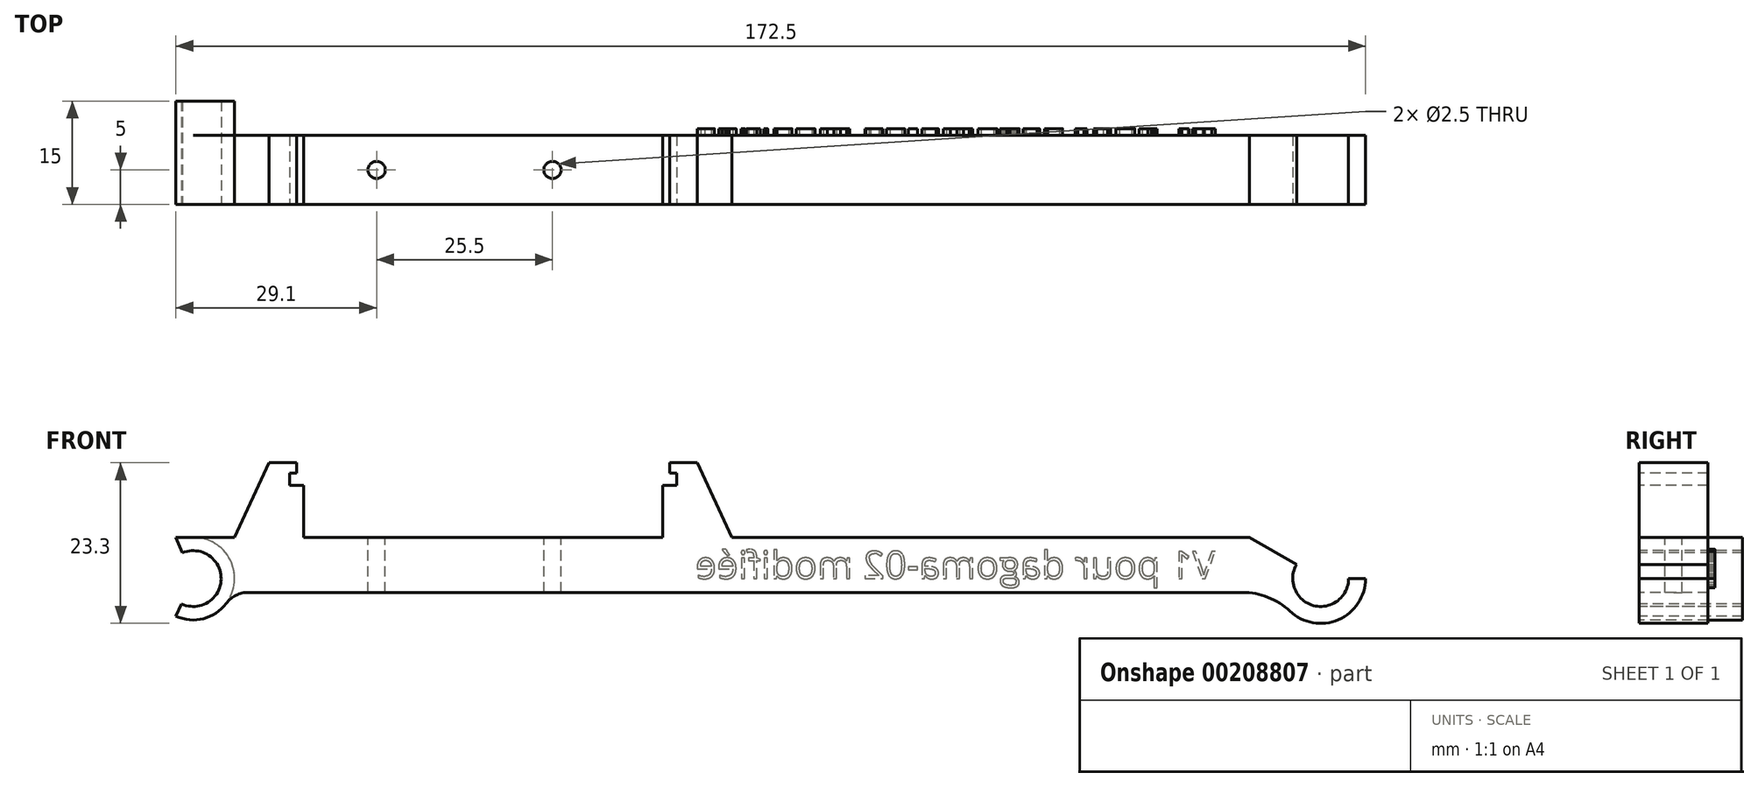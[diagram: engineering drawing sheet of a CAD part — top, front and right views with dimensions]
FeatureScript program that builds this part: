
annotation { "Feature Type Name" : "Feature", "Feature Type Description" : "" }
export const myFeature = defineFeature(function(context is Context, id is Id, definition is map)
    precondition{}
    {
        {
            var Q0;
            Q0=qCreatedBy(makeId("Front.planeOp"),FACE);
            var sketch = newSketch(context, id + "F0", { "sketchPlane" : qUnion([Q0])});
            skArc(sketch, "E0", {"start": v(-1.69, -3.68) * mm, "mid": v(4.05, -0.07) * mm, "end": v(-1.56, 3.74) * mm});
            skArc(sketch, "E1", {"start": v(-2.5, -5.45) * mm, "mid": v(1.48, -5.82) * mm, "end": v(4.8, -3.6) * mm});
            skLineSegment(sketch, "E2", {"start": v(-2.5, 6) * mm, "end": v(6, 6) * mm});
            skLineSegment(sketch, "E3", {"start": v(8, -2) * mm, "end": v(157.32, -2) * mm});
            skLineSegment(sketch, "E4", {"start": v(-1.56, 3.74) * mm, "end": v(-2.5, 6) * mm});
            skLineSegment(sketch, "E5", {"start": v(-1.69, -3.68) * mm, "end": v(-2.5, -5.45) * mm});
            skArc(sketch, "E6.filletArc", {"start": v(8, -2) * mm, "mid": v(6.21, -2.42) * mm, "end": v(4.8, -3.6) * mm});
            skArc(sketch, "E7", {"start": v(0, 6) * mm, "mid": v(5.37, 2.68) * mm, "end": v(4.8, -3.6) * mm});
            skLineSegment(sketch, "E8", {"start": v(16, 6) * mm, "end": v(16, 13.5) * mm});
            skLineSegment(sketch, "E9", {"start": v(16, 13.5) * mm, "end": v(14, 13.5) * mm});
            skLineSegment(sketch, "E10", {"start": v(14, 13.5) * mm, "end": v(14, 15.3) * mm});
            skLineSegment(sketch, "E11", {"start": v(14, 15.3) * mm, "end": v(15, 15.3) * mm});
            skLineSegment(sketch, "E12", {"start": v(15, 15.3) * mm, "end": v(15, 16.8) * mm});
            skLineSegment(sketch, "E13", {"start": v(15, 16.8) * mm, "end": v(11, 16.8) * mm});
            skLineSegment(sketch, "E14", {"start": v(11, 16.8) * mm, "end": v(6, 6) * mm});
            skLineSegment(sketch, "E15", {"start": v(68.1, 6) * mm, "end": v(68.1, 13.5) * mm});
            skLineSegment(sketch, "E16", {"start": v(68.1, 13.5) * mm, "end": v(70.1, 13.5) * mm});
            skLineSegment(sketch, "E17", {"start": v(70.1, 13.5) * mm, "end": v(70.1, 15.3) * mm});
            skLineSegment(sketch, "E18", {"start": v(70.1, 15.3) * mm, "end": v(69.1, 15.3) * mm});
            skLineSegment(sketch, "E19", {"start": v(69.1, 15.3) * mm, "end": v(69.1, 16.8) * mm});
            skLineSegment(sketch, "E20", {"start": v(69.1, 16.8) * mm, "end": v(73.1, 16.8) * mm});
            skLineSegment(sketch, "E21", {"start": v(73.1, 16.8) * mm, "end": v(78.1, 6) * mm});
            skLineSegment(sketch, "E22.trimOffspring", {"start": v(16, 6) * mm, "end": v(68.1, 6) * mm});
            skLineSegment(sketch, "E23.trimOffspring", {"start": v(78.1, 6) * mm, "end": v(153.2, 6) * mm});
            skLineSegment(sketch, "E24", {"start": v(167.55, 0) * mm, "end": v(170, 0) * mm});
            skArc(sketch, "E25", {"start": v(160, 2.04) * mm, "mid": v(162.44, -3.91) * mm, "end": v(167.55, 0) * mm});
            skArc(sketch, "E26", {"start": v(157.32, -2) * mm, "mid": v(164.51, -6.42) * mm, "end": v(170, 0) * mm});
            skLineSegment(sketch, "E27", {"start": v(160, 2.04) * mm, "end": v(153.2, 6) * mm});
            skSolve(sketch);
        }
        {
            var Q0;
            Q0=makeQuery(id+"F0.imprint","IMPRINT",FACE,{"disambiguationData":[TD([[makeQuery(id+"F0.imprint","IMPRINT",EDGE,{"derivedFrom":sQuery(id+"F0.wireOp",EDGE,"E3")}),1.0]])]});
            extrude(context, id + "F1", {"entities" : qUnion([Q0]), "oppositeDirection" : true, "depth" : 10 * mm});
        }
        {
            var Q0;
            {var subQ6=sQuery(id+"F0.wireOp",EDGE,"E0");Q0=makeQuery(id+"F0.imprint","IMPRINT",FACE,{"disambiguationData":[TD([[makeQuery(id+"F0.imprint","IMPRINT",EDGE,{"derivedFrom":subQ6}),-1.0]])]});}
            var Q1;
            {var subQ6=sQuery(id+"F0.wireOp",EDGE,"9NDdW5uR-K7Dr-FAK1-duLJ-1dfglirlA18k");Q1=makeQuery(id+"F0.imprint","IMPRINT",FACE,{"disambiguationData":[TD([[makeQuery(id+"F0.imprint","IMPRINT",EDGE,{"derivedFrom":subQ6}),-1.0]])]});}
            extrude(context, id + "F2", {"entities" : qUnion([Q0, Q1]), "oppositeDirection" : true, "depth" : 15 * mm});
        }
        {
            var Q0;
            Q0=makeQuery(id+"F2.opExtrude","SWEPT_BODY",BODY,{"disambiguationData":[OSD([sQuery(id+"F0.wireOp",EDGE,"E0"),sQuery(id+"F0.wireOp",EDGE,"E1"),sQuery(id+"F0.wireOp",EDGE,"E2"),sQuery(id+"F0.wireOp",EDGE,"E4"),sQuery(id+"F0.wireOp",EDGE,"E5"),sQuery(id+"F0.wireOp",EDGE,"E7")])]});
            var Q1;
            Q1=makeQuery(id+"F1.opExtrude","SWEPT_BODY",BODY,{"disambiguationData":[OSD([sQuery(id+"F0.wireOp",EDGE,"E2"),sQuery(id+"F0.wireOp",EDGE,"E3"),sQuery(id+"F0.wireOp",EDGE,"E6.filletArc"),sQuery(id+"F0.wireOp",EDGE,"E7"),sQuery(id+"F0.wireOp",EDGE,"E8"),sQuery(id+"F0.wireOp",EDGE,"E9"),sQuery(id+"F0.wireOp",EDGE,"E10"),sQuery(id+"F0.wireOp",EDGE,"E11"),sQuery(id+"F0.wireOp",EDGE,"E12"),sQuery(id+"F0.wireOp",EDGE,"E13"),sQuery(id+"F0.wireOp",EDGE,"E14"),sQuery(id+"F0.wireOp",EDGE,"E15"),sQuery(id+"F0.wireOp",EDGE,"E16"),sQuery(id+"F0.wireOp",EDGE,"E17"),sQuery(id+"F0.wireOp",EDGE,"E18"),sQuery(id+"F0.wireOp",EDGE,"E19"),sQuery(id+"F0.wireOp",EDGE,"E20"),sQuery(id+"F0.wireOp",EDGE,"E21"),sQuery(id+"F0.wireOp",EDGE,"E22.trimOffspring"),sQuery(id+"F0.wireOp",EDGE,"E23.trimOffspring"),sQuery(id+"F0.wireOp",EDGE,"E24"),sQuery(id+"F0.wireOp",EDGE,"E25"),sQuery(id+"F0.wireOp",EDGE,"E26"),sQuery(id+"F0.wireOp",EDGE,"E27")])]});
            var Q2;
            Q2=makeQuery(id+"F2v1MvnirLgdYoW_0.opExtrude","SWEPT_BODY",BODY,{"disambiguationData":[OSD([sQuery(id+"F0.wireOp",EDGE,"E3"),sQuery(id+"F0.wireOp",EDGE,"E26"),sQuery(id+"F0.wireOp",EDGE,"y7gqK1Pm-FKcA-JdkN-KHH1-HOYfrpF5GP1K")])]});
            booleanBodies(context, id + "F3", {"operationType" : BooleanOperationType.UNION, "tools" : qUnion([Q0, Q1, Q2])});
        }
        {
            var Q0;
            Q0=makeQuery(id+"F1.opExtrude","SWEPT_FACE",FACE,{"disambiguationData":[OSD([sQuery(id+"F0.wireOp",EDGE,"E22.trimOffspring")])]});
            var sketch = newSketch(context, id + "F4", { "sketchPlane" : qUnion([Q0])});
            skPoint(sketch, "E28", {"position": v(26.6, 5) * mm});
            skPoint(sketch, "E29", {"position": v(52.1, 5) * mm});
            skSolve(sketch);
        }
        {
            var Q0;
            Q0=sQuery(id+"F4.wireOp",VERTEX,"E28");
            var Q1;
            Q1=sQuery(id+"F4.wireOp",VERTEX,"E29");
            var Q2;
            Q2=makeQuery(id+"F2.opExtrude","SWEPT_BODY",BODY,{"disambiguationData":[OSD([sQuery(id+"F0.wireOp",EDGE,"E0"),sQuery(id+"F0.wireOp",EDGE,"E1"),sQuery(id+"F0.wireOp",EDGE,"E2"),sQuery(id+"F0.wireOp",EDGE,"E4"),sQuery(id+"F0.wireOp",EDGE,"E5"),sQuery(id+"F0.wireOp",EDGE,"E7")])]});
            hole(context, id + "F5", {"style" : HoleStyle.SIMPLE, "endStyle" : HoleEndStyle.THROUGH, "holeDiameter" : 2.5 * mm, "locations" : qUnion([Q0, Q1]), "scope" : qUnion([Q2]), "isTappedThrough" : true});
        }
        {
            var Q0;
            Q0=makeQuery(id+"F1.opExtrude","SWEPT_EDGE",EDGE,{"disambiguationData":[OSD([sQuery(id+"F0.wireOp",EDGE,"E3"),sQuery(id+"F0.wireOp",EDGE,"E26")])]});
            fillet(context, id + "F6", {"entities" : qUnion([Q0]), "radius" : 10 * mm, "tangentPropagation" : true, "allowEdgeOverflow" : false});
        }
        {
            var Q0;
            Q0=makeQuery(id+"F1.opExtrude","CAP_FACE",FACE,{"disambiguationData":[OSD([sQuery(id+"F0.wireOp",EDGE,"E2"),sQuery(id+"F0.wireOp",EDGE,"E3"),sQuery(id+"F0.wireOp",EDGE,"E6.filletArc"),sQuery(id+"F0.wireOp",EDGE,"E7"),sQuery(id+"F0.wireOp",EDGE,"E8"),sQuery(id+"F0.wireOp",EDGE,"E9"),sQuery(id+"F0.wireOp",EDGE,"E10"),sQuery(id+"F0.wireOp",EDGE,"E11"),sQuery(id+"F0.wireOp",EDGE,"E12"),sQuery(id+"F0.wireOp",EDGE,"E13"),sQuery(id+"F0.wireOp",EDGE,"E14"),sQuery(id+"F0.wireOp",EDGE,"E15"),sQuery(id+"F0.wireOp",EDGE,"E16"),sQuery(id+"F0.wireOp",EDGE,"E17"),sQuery(id+"F0.wireOp",EDGE,"E18"),sQuery(id+"F0.wireOp",EDGE,"E19"),sQuery(id+"F0.wireOp",EDGE,"E20"),sQuery(id+"F0.wireOp",EDGE,"E21"),sQuery(id+"F0.wireOp",EDGE,"E22.trimOffspring"),sQuery(id+"F0.wireOp",EDGE,"E23.trimOffspring"),sQuery(id+"F0.wireOp",EDGE,"E24"),sQuery(id+"F0.wireOp",EDGE,"E25"),sQuery(id+"F0.wireOp",EDGE,"E26"),sQuery(id+"F0.wireOp",EDGE,"E27")])],"isStart":false});
            var sketch = newSketch(context, id + "F7", { "sketchPlane" : qUnion([Q0])});
            skText(sketch, "E30", { "text": "V1 pour dagoma-02 modifiée", "fontName": "OpenSans-Regular.ttf"});
            const initialGuessF7  = {"E30": [-0.1482, 0, 1, 0, 0.004]};
            skSetInitialGuess(sketch, initialGuessF7);
            skSolve(sketch);
        }
        {
            var Q0;
            Q0=qSketchRegion(id+"F7",true);
            extrude(context, id + "F8", {"entities" : qUnion([Q0]), "operationType" : NewBodyOperationType.ADD, "depth" : 1 * mm});
        }
    });
